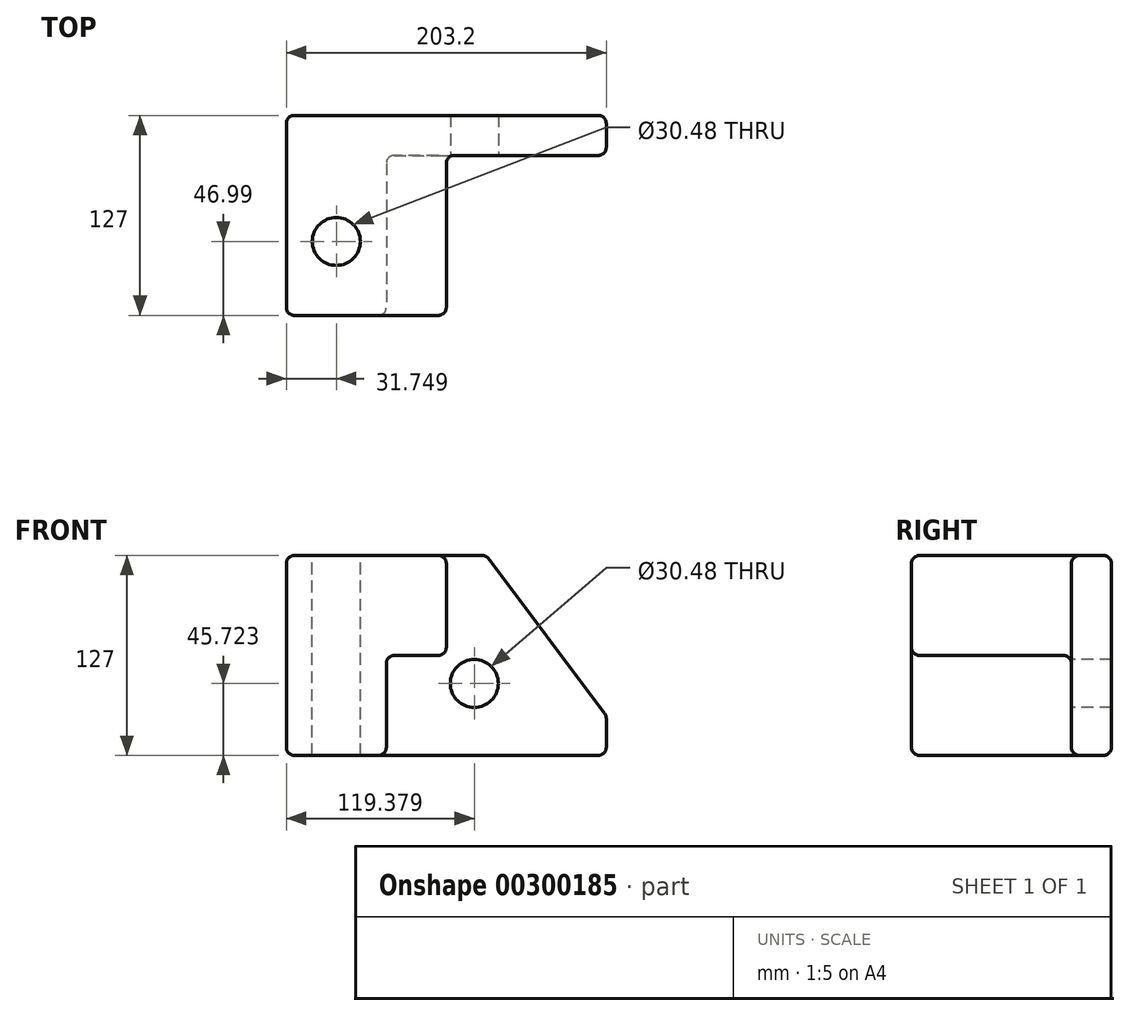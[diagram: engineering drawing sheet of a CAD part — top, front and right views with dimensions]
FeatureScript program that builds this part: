
annotation { "Feature Type Name" : "Feature", "Feature Type Description" : "" }
export const myFeature = defineFeature(function(context is Context, id is Id, definition is map)
    precondition{}
    {
        {
            var Q0;
            Q0=qCreatedBy(makeId("Front.planeOp"),FACE);
            var sketch = newSketch(context, id + "F0", { "sketchPlane" : qUnion([Q0])});
            skLineSegment(sketch, "E0.bottom", {"start": v(-105.73, 67.02) * mm, "end": v(97.47, 67.02) * mm});
            skLineSegment(sketch, "E0.top", {"start": v(-105.73, -59.98) * mm, "end": v(97.47, -59.98) * mm});
            skLineSegment(sketch, "E0.left", {"start": v(-105.73, 67.02) * mm, "end": v(-105.73, -59.98) * mm});
            skLineSegment(sketch, "E0.right", {"start": v(97.47, 67.02) * mm, "end": v(97.47, -59.98) * mm});
            skSolve(sketch);
        }
        {
            var Q0;
            Q0=makeQuery(id+"F0.imprint","IMPRINT",FACE,{"disambiguationData":[TD([[makeQuery(id+"F0.imprint","IMPRINT",EDGE,{"derivedFrom":sQuery(id+"F0.wireOp",EDGE,"E0.bottom")}),-1.0]])]});
            extrude(context, id + "F1", {"entities" : qUnion([Q0]), "depth" : 127 * mm});
        }
        {
            var Q0;
            Q0=makeQuery(id+"F1.opExtrude","CAP_FACE",FACE,{"disambiguationData":[OSD([sQuery(id+"F0.wireOp",EDGE,"E0.bottom"),sQuery(id+"F0.wireOp",EDGE,"E0.top"),sQuery(id+"F0.wireOp",EDGE,"E0.left"),sQuery(id+"F0.wireOp",EDGE,"E0.right")])],"isStart":false});
            var sketch = newSketch(context, id + "F2", { "sketchPlane" : qUnion([Q0])});
            skLineSegment(sketch, "E1", {"start": v(-105.73, 67.02) * mm, "end": v(-4.13, 67.02) * mm});
            skLineSegment(sketch, "E2", {"start": v(-4.13, 67.02) * mm, "end": v(-4.13, 3.52) * mm});
            skLineSegment(sketch, "E3", {"start": v(-4.13, 3.52) * mm, "end": v(-42.23, 3.52) * mm});
            skLineSegment(sketch, "E4", {"start": v(-42.23, 3.52) * mm, "end": v(-42.23, -59.98) * mm});
            skLineSegment(sketch, "E5", {"start": v(-42.23, -59.98) * mm, "end": v(-105.73, -59.98) * mm});
            skLineSegment(sketch, "E6", {"start": v(-105.73, -59.98) * mm, "end": v(-105.73, 67.02) * mm});
            skSolve(sketch);
        }
        {
            var Q0;
            {var subQ3=sQuery(id+"F2.wireOp",EDGE,"E2");Q0=makeQuery(id+"F2.imprint","IMPRINT",FACE,{"disambiguationData":[TD([[makeQuery(id+"F2.imprint","IMPRINT",EDGE,{"derivedFrom":subQ3}),1.0]])]});}
            extrude(context, id + "F3", {"entities" : qUnion([Q0]), "operationType" : NewBodyOperationType.REMOVE, "oppositeDirection" : true, "depth" : 101.6 * mm});
        }
        {
            var Q0;
            Q0=makeQuery(id+"F1.opExtrude","SWEPT_EDGE",EDGE,{"disambiguationData":[OSD([sQuery(id+"F0.wireOp",EDGE,"E0.bottom"),sQuery(id+"F0.wireOp",EDGE,"E0.right")])]});
            chamfer(context, id + "F4", {"entities" : qUnion([Q0]), "chamferType" : ChamferType.TWO_OFFSETS, "width1" : 76.2 * mm, "oppositeDirection" : false, "width2" : 101.6 * mm, "tangentPropagation" : true});
        }
        {
            var Q0;
            Q0=makeQuery(id+"F1.opExtrude","SWEPT_FACE",FACE,{"disambiguationData":[OSD([sQuery(id+"F0.wireOp",EDGE,"E0.bottom")])]});
            var Q1;
            Q1=makeQuery(id+"F1.opExtrude","CAP_FACE",FACE,{"disambiguationData":[OSD([sQuery(id+"F0.wireOp",EDGE,"E0.bottom"),sQuery(id+"F0.wireOp",EDGE,"E0.top"),sQuery(id+"F0.wireOp",EDGE,"E0.left"),sQuery(id+"F0.wireOp",EDGE,"E0.right")])],"isStart":false});
            var Q2;
            Q2=makeQuery(id+"F3.boolean.opBoolean","COPY",FACE,{"derivedFrom":makeQuery(id+"F3.opExtrude","SWEPT_FACE",FACE,{"disambiguationData":[OSD([sQuery(id+"F2.wireOp",EDGE,"E2")])]})});
            var Q3;
            Q3=makeQuery(id+"F3.boolean.opBoolean","COPY",FACE,{"derivedFrom":makeQuery(id+"F3.opExtrude","SWEPT_FACE",FACE,{"disambiguationData":[OSD([sQuery(id+"F2.wireOp",EDGE,"E4")])]})});
            var Q4;
            Q4=makeQuery(id+"F3.boolean.opBoolean","COPY",FACE,{"derivedFrom":makeQuery(id+"F3.opExtrude","CAP_FACE",FACE,{"disambiguationData":[OSD([sQuery(id+"F0.wireOp",EDGE,"E0.bottom"),sQuery(id+"F0.wireOp",EDGE,"E0.top"),sQuery(id+"F0.wireOp",EDGE,"E0.right"),sQuery(id+"F2.wireOp",EDGE,"E2"),sQuery(id+"F2.wireOp",EDGE,"E3"),sQuery(id+"F2.wireOp",EDGE,"E4")])],"isStart":false})});
            var Q5;
            Q5=makeQuery(id+"F4.opChamfer","BLEND_FACE",FACE,{"disambiguationData":[OSD([sQuery(id+"F0.wireOp",EDGE,"E0.bottom"),sQuery(id+"F0.wireOp",EDGE,"E0.right")])]});
            var Q6;
            Q6=makeQuery(id+"F1.opExtrude","SWEPT_FACE",FACE,{"disambiguationData":[OSD([sQuery(id+"F0.wireOp",EDGE,"E0.right")])]});
            var Q7;
            Q7=makeQuery(id+"F1.opExtrude","SWEPT_FACE",FACE,{"disambiguationData":[OSD([sQuery(id+"F0.wireOp",EDGE,"E0.left")])]});
            var Q8;
            Q8=makeQuery(id+"F1.opExtrude","CAP_FACE",FACE,{"disambiguationData":[OSD([sQuery(id+"F0.wireOp",EDGE,"E0.bottom"),sQuery(id+"F0.wireOp",EDGE,"E0.top"),sQuery(id+"F0.wireOp",EDGE,"E0.left"),sQuery(id+"F0.wireOp",EDGE,"E0.right")])],"isStart":true});
            var Q9;
            Q9=makeQuery(id+"F1.opExtrude","SWEPT_FACE",FACE,{"disambiguationData":[OSD([sQuery(id+"F0.wireOp",EDGE,"E0.top")])]});
            fillet(context, id + "F5", {"entities" : qUnion([Q0, Q1, Q2, Q3, Q4, Q5, Q6, Q7, Q8, Q9]), "radius" : 5.08 * mm, "tangentPropagation" : true, "allowEdgeOverflow" : false});
        }
        {
            var Q0;
            Q0=makeQuery(id+"F3.boolean.opBoolean","COPY",FACE,{"derivedFrom":makeQuery(id+"F3.opExtrude","CAP_FACE",FACE,{"disambiguationData":[OSD([sQuery(id+"F0.wireOp",EDGE,"E0.bottom"),sQuery(id+"F0.wireOp",EDGE,"E0.top"),sQuery(id+"F0.wireOp",EDGE,"E0.right"),sQuery(id+"F2.wireOp",EDGE,"E2"),sQuery(id+"F2.wireOp",EDGE,"E3"),sQuery(id+"F2.wireOp",EDGE,"E4")])],"isStart":false})});
            var sketch = newSketch(context, id + "F6", { "sketchPlane" : qUnion([Q0])});
            skCircle(sketch, "E7", {"center": v(13.65, -14.26) * mm, "radius": 15.24 * mm});
            skSolve(sketch);
        }
        {
            var Q0;
            Q0=makeQuery(id+"F6.imprint","IMPRINT",FACE,{"disambiguationData":[TD([[makeQuery(id+"F6.imprint","IMPRINT",EDGE,{"derivedFrom":sQuery(id+"F6.wireOp",EDGE,"E7")}),1.0]])]});
            extrude(context, id + "F7", {"entities" : qUnion([Q0]), "operationType" : NewBodyOperationType.REMOVE, "oppositeDirection" : true, "depth" : 25.4 * mm});
        }
        {
            var Q0;
            Q0=makeQuery(id+"F1.opExtrude","SWEPT_FACE",FACE,{"disambiguationData":[OSD([sQuery(id+"F0.wireOp",EDGE,"E0.bottom")])]});
            var sketch = newSketch(context, id + "F8", { "sketchPlane" : qUnion([Q0])});
            skCircle(sketch, "E8", {"center": v(-73.98, -80) * mm, "radius": 15.24 * mm});
            skSolve(sketch);
        }
        {
            var Q0;
            Q0=makeQuery(id+"F8.imprint","IMPRINT",FACE,{"disambiguationData":[TD([[makeQuery(id+"F8.imprint","IMPRINT",EDGE,{"derivedFrom":sQuery(id+"F8.wireOp",EDGE,"E8")}),1.0]])]});
            extrude(context, id + "F9", {"entities" : qUnion([Q0]), "operationType" : NewBodyOperationType.REMOVE, "oppositeDirection" : true, "depth" : 127 * mm});
        }
    });
